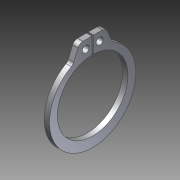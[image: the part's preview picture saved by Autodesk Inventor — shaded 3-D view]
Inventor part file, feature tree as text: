
AUTODESK INVENTOR PART (.ipt)
format: ipt  version: 2014 SP1 (Build 180222100, 222)  size: 107,008 bytes
history: native  units: in
note: dims shown in document units (in); Inventor stores cm internally (conversion verified against a paired STEP export)
features: fillet x1, other x1, imported_body x1
ambient origin geometry x8: Origin, YZ Plane, XZ Plane, XY Plane, X Axis, Y Axis, Z Axis, Center Point
bodies: Body1 (feature_tree)
feature tree (3):
  fillet  "Fillet1"  [1 undecoded]
  other  "217-3421-011 Rev2_97633A200.ipt1"
  imported_body  "Base1"
note: 1 required parameter value undecoded (feature->parameter linkage not recoverable at this tier; creation-order binding heuristic only, values carry confidence <= 0.55)
